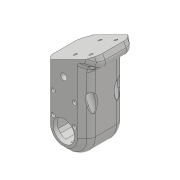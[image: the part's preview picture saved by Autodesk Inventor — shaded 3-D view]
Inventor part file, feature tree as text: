
AUTODESK INVENTOR PART (.ipt)
format: ipt  version: 2018 (Build 220112000, 112)  size: 1,022,976 bytes
history: native  units: mm
features: sketch x30, projected_geometry x26, extrude x23, hole x10, fillet x10, chamfer x3, mirror x1, plane x1
ambient origin geometry x8: Origin, YZ Plane, XZ Plane, XY Plane, X Axis, Y Axis, Z Axis, Center Point
bodies: Solid1 (feature_tree)
feature tree (104):
  extrude  "Extrusion1"  Depth=45.0mm
  extrude  "Extrusion2"  Depth=2.25mm
  hole  "Hole1"  [1 undecoded]
  hole  "Hole2"  [1 undecoded]
  fillet  "Fillet1"  Radius=14.0mm
  extrude  "Extrusion3"  Depth=18.5mm
  extrude  "Extrusion4"  Depth=10.0mm
  extrude  "Extrusion5"  Depth=2.0mm
  extrude  "Extrusion6"  Depth=2.0mm
  hole  "Hole3"  [1 undecoded]
  extrude  "Extrusion7"  Depth=0.5mm
  extrude  "Extrusion8"  Depth=5.0mm TaperAngle=0.0deg
  extrude  "Extrusion9"  Depth=10.0mm
  extrude  "Extrusion10"  Depth=10.0mm
  extrude  "Extrusion11"  Depth=14.5mm
  extrude  "Extrusion12"  Depth=20.0mm
  extrude  "Extrusion13"  Depth=5.0mm
  extrude  "Extrusion14"  Depth=2.25mm
  extrude  "Extrusion15"  Depth=5.0mm
  extrude  "Extrusion16"  Depth=9.0mm
  extrude  "Extrusion17"  Depth=1.0mm
  chamfer  "Chamfer1"  Distance=1.0mm
  fillet  "Fillet7"  Radius=20.7mm
  fillet  "Fillet8"  Radius=32.0mm
  mirror  "Mirror1"
  extrude  "Extrusion24"  Depth=1.0mm TaperAngle=0.0deg
  extrude  "Extrusion25"  Depth=8.0mm
  extrude  "Extrusion26"  Depth=0.2mm TaperAngle=0.0deg
  extrude  "Extrusion27"  Depth=0.5mm TaperAngle=0.0deg
  extrude  "Extrusion28"  Depth=5.0mm TaperAngle=0.0deg
  chamfer  "Chamfer5"  Distance=5.0mm
  fillet  "Fillet18"  Radius=0.2mm
  fillet  "Fillet19"  Radius=0.2mm
  extrude  "Extrusion29"  Depth=2.0mm
  chamfer  "Chamfer6"  Distance=40.0mm
  hole  "Hole10"  [1 undecoded]
  plane  "Work Plane2"
  hole  "Hole11"  [1 undecoded]
  fillet  "Fillet20"  Radius=10.0mm
  sketch  "Sketch43"  dims[d102=2.5mm d103=2.0mm d104=45.0deg d105=1.5mm]
  hole  "Hole12"  [1 undecoded]
  hole  "Hole13"  [1 undecoded]
  hole  "Hole14"  [1 undecoded]
  fillet  "Fillet21"  Radius=8.0mm
  fillet  "Fillet22"  Radius=10.0mm
  hole  "Hole15"  [1 undecoded]
  fillet  "Fillet23"  Radius=2.0mm
  hole  "Hole16"  [1 undecoded]
  fillet  "Fillet24"  Radius=8.0mm
  sketch  "Sketch1"  dims[d0=24.5mm d1=45.0mm]
  sketch  "Sketch2"  dims[d2=1.95mm d3=0.0mm d4=2.25mm]
  projected_geometry  "Projected Loop1"
  sketch  "Sketch3"  dims[d5=20.0mm d6=2.25mm]
  projected_geometry  "Projected Loop2"
  sketch  "Sketch4"  dims[d7=5.25mm d8=5.25mm d9=14.0mm]
  projected_geometry  "Projected Loop3"
  sketch  "Sketch5"  dims[d10=5.25mm d11=18.5mm]
  projected_geometry  "Projected Loop4"
  sketch  "Sketch6"  dims[d12=10.0mm d13=0.0mm d14=20.5mm]
  projected_geometry  "Projected Loop5"
  sketch  "Sketch7"  dims[d15=2.0mm d16=2.195mm]
  projected_geometry  "Projected Loop6"
  sketch  "Sketch8"  dims[d17=2.0mm]
  projected_geometry  "Projected Loop7"
  sketch  "Sketch9"  dims[d18=2.4mm d19=6.0mm d20=4.4mm d21=2.0mm d22=90.0deg d23=8.0mm d24=20.594885mm d25=20.5mm]
  projected_geometry  "Projected Loop8"
  projected_geometry  "Projected Loop9"
  sketch  "Sketch10"  dims[d26=26.65mm d27=2.0mm]
  projected_geometry  "Projected Loop10"
  projected_geometry  "Projected Loop11"
  sketch  "Sketch11"  dims[d28=2.0mm]
  projected_geometry  "Projected Loop12"
  sketch  "Sketch12"  dims[d29=2.4mm d30=6.0mm d31=4.4mm d32=2.0mm d33=90.0deg d34=8.0mm d35=20.594885mm d36=0.5mm]
  sketch  "Sketch13"  dims[d37=18.0mm d38=5.0mm d39=0.0mm]
  sketch  "Sketch14"  dims[d41=10.0mm d42=0.0mm d43=24.5mm]
  projected_geometry  "Projected Loop13"
  sketch  "Sketch15"  dims[d44=1.15mm d45=0.0mm d46=10.0mm]
  sketch  "Sketch16"  dims[d47=21.0mm d48=14.5mm]
  projected_geometry  "Projected Loop14"
  sketch  "Sketch17"  dims[d49=20.0mm d50=14.5mm]
  projected_geometry  "Projected Loop15"
  sketch  "Sketch18"  dims[d51=24.5mm d52=5.0mm]
  projected_geometry  "Projected Loop16"
  sketch  "Sketch19"  dims[d53=5.0mm d54=2.25mm]
  projected_geometry  "Projected Loop17"
  sketch  "Sketch20"  dims[d55=2.25mm d56=5.0mm]
  projected_geometry  "Projected Loop18"
  sketch  "Sketch35"  dims[d57=5.0mm d58=9.0mm]
  projected_geometry  "Projected Loop28"
  sketch  "Sketch36"  dims[d59=14.75mm d60=4.0mm d61=1.0mm d62=0.0mm d63=20.7mm]
  projected_geometry  "Projected Loop29"
  sketch  "Sketch37"  dims[d64=2.4mm d65=6.0mm d66=4.4mm d67=2.0mm d68=90.0deg d69=8.0mm d70=20.594885mm d72=32.0mm]
  sketch  "Sketch38"  dims[d73=5.0mm d74=0.0mm d75=1.0mm d76=0.0mm]
  sketch  "Sketch39"  dims[d77=12.25mm d78=0.0mm d80=8.0mm]
  projected_geometry  "Projected Loop30"
  sketch  "Sketch40"  dims[d81=4.5mm d82=0.0mm d84=0.2mm d85=0.0mm]
  projected_geometry  "Projected Loop31"
  sketch  "Sketch41"  dims[d86=21.0mm d87=0.5mm d88=0.0mm]
  projected_geometry  "Projected Loop32"
  projected_geometry  "Projected Loop33"
  sketch  "Sketch42"  dims[d91=8.0mm d92=0.0mm d93=5.0mm d94=0.0mm d95=5.0mm d96=0.0mm d98=0.2mm d99=0.0mm d100=0.2mm d101=0.0mm]
  projected_geometry  "Projected Loop34"
  sketch  "Sketch44"  dims[d114=0.5mm d187=40.0mm d188=70.0mm d189=20.0mm d190=10.0mm d191=0.0mm d192=10.0mm d193=0.0mm d194=2.0mm d195=0.0mm d196=2.0mm d197=0.0mm d198=8.0mm d199=10.0mm d200=2.0mm d201=0.0mm d204=7.0mm d205=2.0mm d206=45.0deg d207=5.0mm d208=8.0mm d209=15.0mm d210=2.0mm d211=0.0mm d212=1.5mm d213=2.0mm d214=45.0deg d215=24.0mm d216=17.0mm d217=3.5mm d218=3.2mm d219=6.0mm d220=9.4mm d221=2.0mm d222=90.0deg d223=8.0mm d224=20.594885mm d225=6.0mm d226=6.0mm d227=9.4mm d228=2.0mm d229=90.0deg d230=69.0mm d231=0.0mm d232=1.0mm d233=8.0mm d234=2.459mm d235=6.0mm d236=9.4mm d237=2.0mm d238=90.0deg d239=34.0mm d240=20.594885mm d241=3.2mm d242=6.0mm d243=6.3mm d244=2.0mm d245=90.0deg d246=20.55mm d247=0.0mm d248=6.0mm d249=6.0mm d250=6.3mm d251=2.0mm d252=90.0deg d253=10.0mm d254=0.0mm d255=1.5mm d256=0.75mm d257=4.0mm d258=6.0mm d259=4.4mm d260=2.0mm d261=90.0deg d262=2.5mm d263=0.0mm d264=1.0mm d265=4.0mm d266=6.0mm d267=4.4mm d268=2.0mm d269=90.0deg d270=2.5mm d271=0.0mm d272=1.0mm]
  projected_geometry  "Projected Loop35"
note: 10 required parameter values undecoded (feature->parameter linkage not recoverable at this tier; creation-order binding heuristic only, values carry confidence <= 0.55)
